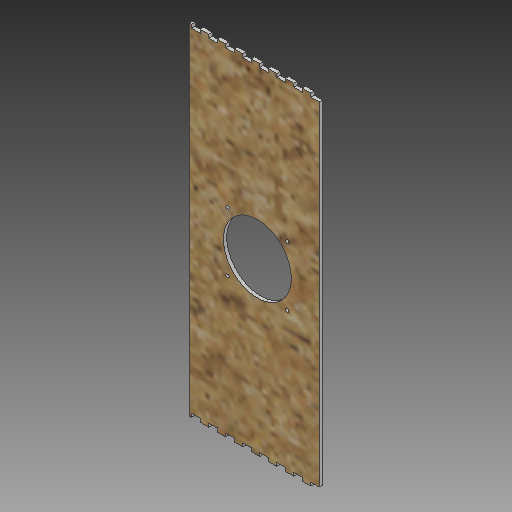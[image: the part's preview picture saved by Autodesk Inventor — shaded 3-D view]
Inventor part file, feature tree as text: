
AUTODESK INVENTOR PART (.ipt)
format: ipt  version: 2019 (Build 230136000, 136)  size: 282,624 bytes
history: native  units: mm
features: reference x5, other x4, extrude x2, sketch x2
ambient origin geometry x8: Origin, YZ Plane, XZ Plane, XY Plane, X Axis, Y Axis, Z Axis, Center Point
bodies: Body1 (feature_tree)
feature tree (13):
  other  "Твердое тело1"
  extrude  "Выдавливание1"  Depth=400.0mm
  extrude  "Выдавливание2"  Depth=200.0mm
  sketch  "Эскиз1"
  reference  "Ссылка1"
  reference  "Ссылка2"
  reference  "Ссылка3"
  reference  "Ссылка4"
  reference  "Ссылка5"
  sketch  "Эскиз3"
  parser-record x1  (decoder bookkeeping rows leaked as tree rows — omitted from the tree; the rows remain in map.json)
  other  "kowsh.iam"
  other  "mot37:1"
note: 1 file-system path scrubbed to <path> (originals preserved in map.json)
